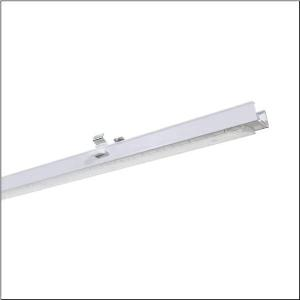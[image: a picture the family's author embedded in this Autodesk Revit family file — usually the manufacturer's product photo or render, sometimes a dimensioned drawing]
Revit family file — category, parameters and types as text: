
# Revit family: trunking_flex_31_51re12mb4cb
name_source: partatom
category: Lighting Fixtures
units: mm (PartAtom-declared; Revit-internal decimal feet)

## family parameters
Cut with Voids When Loaded = No
Host = Face
Light Source = No
Part Type = Normal
Room Calculation Point = No
Round Connector Dimension = Use Diameter
Shared = No

## types (1)
- --- (1 x LED, 11500 lm, 66 W, 4000K)
    Apparent Load = 66 VA
    CIE Flux Codes = 65 91 98 99 100
    Color Rendering = 80
    Color Temperature = 4000K
    Default Elevation = 1800 mm
    Description = Trunking Flex 31, luminaire insert, of extruded aluminium section, coated, traffic white (RAL 9016), length: 1.472mm, width: 91mm, height: 53mm, LED rated luminous flux: 11.500lm, light colour: 840, control gear: ON/OFF Multilumen, with system connector: socket, mains connection: 220..240V, AC, 50/60Hz, rated input power: 66W, connected load according to luminous flux setting (19/24/32/37/47/52/60/66W), luminous flux adjustable on luminaire in eight steps (3450/4380/5800/6700/8350/9200/10500/11500lm ), primary light control with lens, of plastic, primary optical cover: cover, of PMMA, light emission: direct distribution, protection rating (complete): IP20, insulation class (complete): insulation class I (protective earthing), certification: CE, UKCA, impact resistance: IK02, permissible ambient temperature for indoor applications: -20..+40°C, packaging unit: 1 piece
    Height = 58 mm
    Lamp = 1 x LED
    Lamp Light Flux = 11500 lm
    Lamp Power = 66 W
    Lamp count = 1
    Length = 1472 mm
    Luminous efficacy = 174 lm/W
    Manufacturer = Siteco
    ModVariant = No
    Model = 51RE12MB4CB
    Mounting Place = Ceiling
    Mounting Type = Pendant
    Number of Poles = 1
    OnlyDefault = Yes
    Power Factor = 1
    Product Name = Trunking Flex 31
    Product group = luminaire insert
    ProductGroupID = 901
    Protection Class = Protection class I
    Protection Degree = IP 20
    RLX_Detail_Level = 1
    RLX_Emergency_Light_Flux = 0 lm
    RLX_Emergency_Type = 0
    RLX_Emergency_Type_DB = No
    RlxData = <blob elided: 20993 chars, md5=09b7da8b>
    Socket = socket
    Standby Power = 0 W
    System Light Flux = 11500 lm
    System Power = 66 W
    Type Comments = factory setting: luminous flux: 100 % | (ON | ON | ON)
    Type Image = l_1266702.jpg
    URL = http://relux.com
    VarID = @adj_018641
    Voltage = 0 V
    Weight = 0.00 kg
    Width = 65 mm

## geometry (parser evidence)
native form markers: Blend x4, Sweep x11
no freeform markers — native parametric forms only
